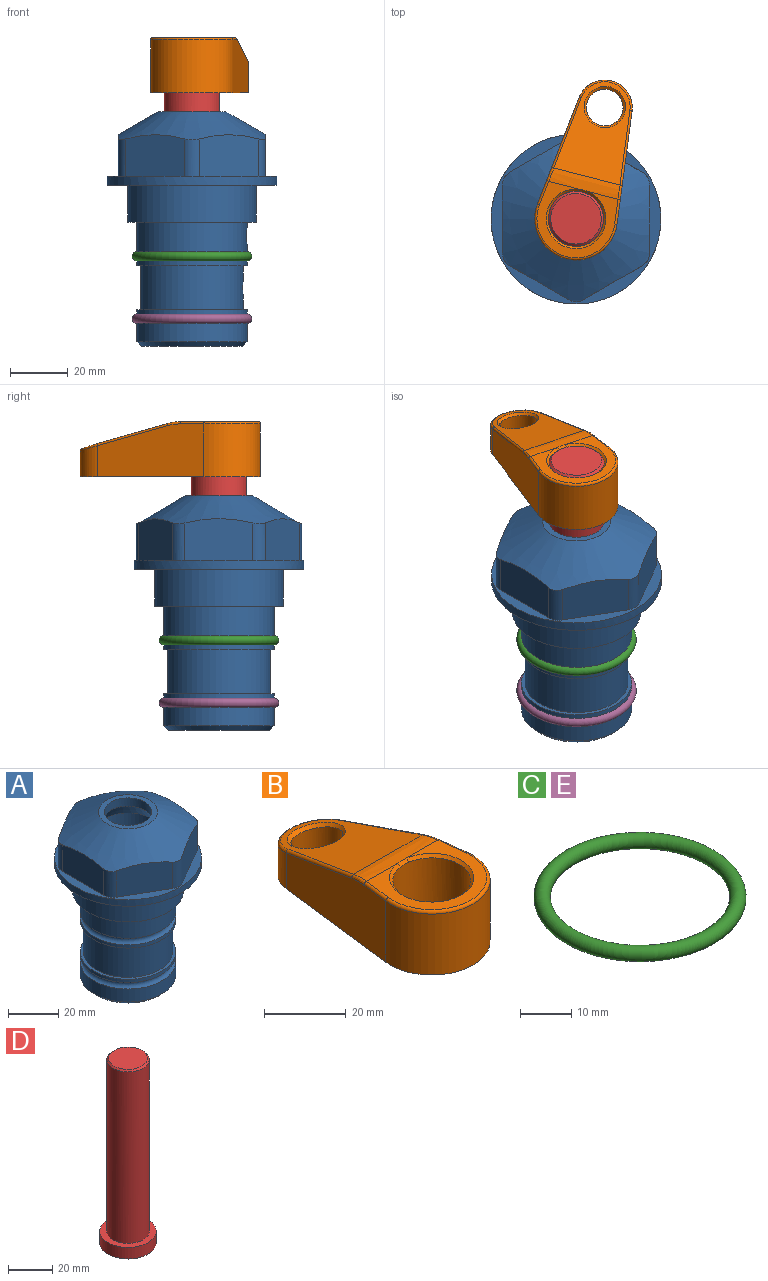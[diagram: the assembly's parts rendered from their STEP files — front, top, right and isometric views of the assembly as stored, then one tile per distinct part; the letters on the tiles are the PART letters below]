
ASSEMBLY  parts=5 mates=4
PART A: 36 faces, bbox 58.7x58.7x81 mm
  f0: cylinder r=17.78mm len=35.56mm, axis (0,0,1), area 1670.8mm2, adj f23,f24,f31
  f1: cylinder r=19.05mm len=38.1mm, axis (0,0,1), area 1191.9mm2, adj f26,f27,f30
  f2: plane 58.66x58.66mm, normal (0,0,-1), area 1150.6mm2, adj f3,f28
  f3: cylinder r=29.33mm len=58.66mm, axis (0,0,-1), area 585.1mm2, adj f2,f4
  f4: plane 58.66x58.66mm, normal (0,0,1), area 475.9mm2, adj f3,f5,f6,f7,f8,f9,f10,f11
  f5: plane 20.32x14.34mm, normal (-0.5,0.87,0), area 324.4mm2, adj f4,f15,f16,f17
  f6: plane 20.32x14.34mm, normal (0.5,0.87,0), area 324.4mm2, adj f4,f14,f15,f17
  f7: plane 23.48x14.34mm, normal (1,0,0), area 324.4mm2, adj f4,f13,f14,f17
  f8: plane 20.32x14.34mm, normal (0.5,-0.87,0), area 324.4mm2, adj f4,f12,f13,f17
  f9: plane 20.32x14.34mm, normal (-0.5,-0.87,0), area 324.4mm2, adj f4,f11,f12,f17
  f10: plane 23.48x14.34mm, normal (-1,0,0), area 324.4mm2, adj f4,f11,f16,f17
  f11: cylinder r=5.08mm len=12.85mm, axis (0,0,-1), area 67.2mm2, adj f4,f9,f10,f17
  f12: cylinder r=5.08mm len=12.85mm, axis (0,0,-1), area 67.2mm2, adj f4,f8,f9,f17
  f13: cylinder r=5.08mm len=12.85mm, axis (0,0,-1), area 67.2mm2, adj f4,f7,f8,f17
  f14: cylinder r=5.08mm len=12.85mm, axis (0,0,-1), area 67.2mm2, adj f4,f6,f7,f17
  f15: cylinder r=5.08mm len=12.85mm, axis (0,0,-1), area 67.2mm2, adj f4,f5,f6,f17
  f16: cylinder r=5.08mm len=12.85mm, axis (0,0,-1), area 67.2mm2, adj f4,f5,f10,f17
  f17: cone r=11.73mm half-angle=60deg, axis (0,0,-1), area 2071.8mm2, adj f5,f6,f7,f8,f9,f10,f11,f12
  f18: plane 23.46x23.46mm, normal (0,0,1), area 147.4mm2, adj f17,f35
  f19: plane 34.93x34.93mm, normal (0,0,-1), area 958mm2, adj f29
  f20: cylinder r=19.05mm len=38.1mm, axis (0,0,1), area 760.1mm2, adj f21,f29
  f21: torus R=19.05mm, axis (0,0,1), area 565.3mm2, adj f20,f22
  f22: cylinder r=19.05mm len=38.1mm, axis (0,0,1), area 190mm2, adj f21,f23
  f23: plane 38.1x38.1mm, normal (0,0,1), area 146.9mm2, adj f0,f22
  f24: plane 38.1x38.1mm, normal (0,0,-1), area 146.9mm2, adj f0,f25
  f25: cylinder r=19.05mm len=38.1mm, axis (0,0,1), area 190mm2, adj f24,f26
  f26: torus R=19.05mm, axis (0,0,1), area 565.3mm2, adj f1,f25
  f27: plane 44.45x44.45mm, normal (0,0,-1), area 411.7mm2, adj f1,f28
  f28: cylinder r=22.23mm len=44.45mm, axis (0,0,1), area 1773.5mm2, adj f2,f27
  f29: cone r=19.05mm half-angle=45deg, axis (0,0,1), area 257.5mm2, adj f19,f20
  f30: cylinder r=3.17mm len=6.75mm, axis (-1,0,0), area 128mm2, adj f1,f33
  f31: cylinder r=3.17mm len=6.35mm, axis (-1,0,0), area 102.5mm2, adj f0,f33
  f32: plane 25.4x25.4mm, normal (0,0,1), area 506.7mm2, adj f33
  f33: cylinder r=12.7mm len=66.42mm, axis (0,0,-1), area 5236.2mm2, adj f30,f31,f32,f34
  f34: cone r=9.53mm half-angle=30deg, axis (0,0,-1), area 443.4mm2, adj f33,f35
  f35: cylinder r=9.53mm len=19.05mm, axis (0,0,-1), area 240.9mm2, adj f18,f34
PART B: 31 faces, bbox 31.7x65.5x19.8 mm
  f0: plane 39.12x18.26mm, normal (0.99,0.12,0), area 612.2mm2, adj f1,f4,f7,f11,f13,f15
  f1: cylinder r=9.53mm len=18.91mm, axis (0,0,-1), area 296.1mm2, adj f0,f2,f7,f17
  f2: plane 39.12x18.26mm, normal (-0.99,0.12,0), area 612.2mm2, adj f1,f4,f7,f12,f14,f16
  f3: cylinder r=6.35mm len=12.7mm, axis (0,0,-1), area 362.4mm2, adj f7,f18
  f4: cylinder r=14.29mm len=28.58mm, axis (0,0,-1), area 882.2mm2, adj f0,f2,f7,f10
  f5: cylinder r=9.53mm len=19.05mm, axis (0,0,-1), area 1092.6mm2, adj f7,f19,f20
  f6: plane 26.99x23.69mm, normal (0,0,1), area 216.2mm2, adj f9,f10,f11,f12,f19
  f7: plane 63.5x28.58mm, normal (0,0,-1), area 661.8mm2, adj f0,f1,f2,f3,f4,f5,f22,f23
  f8: plane 33.52x23.6mm, normal (0,0.26,0.97), area 486mm2, adj f9,f15,f16,f17,f18
  f9: cylinder r=19.05mm len=24.72mm, axis (1,0,0), area 120.4mm2, adj f6,f8,f13,f14,f20
  f10: torus R=13.49mm, axis (0,0,1), area 59mm2, adj f4,f6,f11,f12
  f11: cylinder r=0.79mm len=8.67mm, axis (0.12,-0.99,0), area 10.8mm2, adj f0,f6,f10,f13
  f12: cylinder r=0.79mm len=8.67mm, axis (0.12,0.99,0), area 10.8mm2, adj f2,f6,f10,f14
  f13: bspline ~4.95x1.42mm, area 6.1mm2, adj f0,f9,f11,f15
  f14: bspline ~4.95x1.42mm, area 6.1mm2, adj f2,f9,f12,f16
  f15: cylinder r=0.79mm len=25.95mm, axis (0.12,-0.96,0.26), area 32.9mm2, adj f0,f8,f13,f17
  f16: cylinder r=0.79mm len=25.95mm, axis (0.12,0.96,-0.26), area 32.9mm2, adj f2,f8,f14,f17
  f17: bspline ~18.91x8.38mm, area 30mm2, adj f1,f8,f15,f16
  f18: bspline ~14.29x14.29mm, area 48.3mm2, adj f3,f8
  f19: cone r=9.53mm half-angle=45deg, axis (0,0,1), area 66.5mm2, adj f5,f6,f20
  f20: bspline ~3.22x0.96mm, area 3.5mm2, adj f5,f9,f19
  f21: plane 2.75x2.72mm, normal (0,0,-1), area 2.9mm2, adj f23,f25,f28
  f22: plane 23.05x15.88mm, normal (-0.99,-0.12,0), area 323.6mm2, adj f7,f25,f26,f27,f28,f29
  f23: plane 23.05x15.88mm, normal (0.99,-0.12,0), area 323.6mm2, adj f7,f21,f25,f27,f28,f30
  f24: cylinder r=9.53mm len=10.69mm, axis (0,0,-1), area 114.7mm2, adj f7,f27,f29,f30
  f25: cylinder r=12.7mm len=20.59mm, axis (0,0,-1), area 381.1mm2, adj f7,f21,f22,f23,f26,f28
  f26: plane 2.75x2.72mm, normal (0,0,-1), area 2.9mm2, adj f22,f25,f28
  f27: plane 19.72x18.37mm, normal (0,-0.26,-0.97), area 291.8mm2, adj f22,f23,f24,f28,f29,f30
  f28: cylinder r=15.88mm len=19.92mm, axis (1,0,0), area 54.8mm2, adj f21,f22,f23,f25,f26,f27
  f29: cylinder r=1.59mm len=11mm, axis (0,0,-1), area 34.7mm2, adj f7,f22,f24,f27
  f30: cylinder r=1.59mm len=11mm, axis (0,0,-1), area 34.7mm2, adj f7,f23,f24,f27
PART C: 1 faces, bbox 44.7x44.7x3.2 mm
  f0: torus R=19.05mm, axis (0,0,1), area 1193.9mm2
PART D: 6 faces, bbox 25.4x25.4x101.6 mm
  f0: plane 17.46x17.46mm, normal (0,0,1), area 239.5mm2, adj f5
  f1: plane 25.4x25.4mm, normal (0,0,-1), area 506.7mm2, adj f2
  f2: cylinder r=12.7mm len=25.4mm, axis (0,0,1), area 506.7mm2, adj f1,f3
  f3: plane 25.4x25.4mm, normal (0,0,1), area 221.7mm2, adj f2,f4
  f4: cylinder r=9.53mm len=94.46mm, axis (0,0,1), area 5653mm2, adj f3,f5
  f5: cone r=8.73mm half-angle=45deg, axis (0,0,-1), area 64.4mm2, adj f0,f4
PART E: same geometry as C
PLACE A at identity fixed
PLACE B rot(axis=(0,0,-1),14.5deg) t=(0,0,-12.45)mm
PLACE C at identity
PLACE D rot(axis=(0,0,-1),14.5deg) t=(0,0,-12.45)mm
PLACE E t=(0,0,-21.59)mm
MATE fastened E.f0 <-> A.f0  axis (0,0,1) through (0,0,-46.1)mm
MATE fastened C.f0 <-> A.f0  axis (0,0,1) through (0,0,-24.51)mm
MATE cylindrical D.f2 <-> A.f0  axis (0,0,-1) through (0,0,-50.55)mm
MATE fastened B.f4 <-> D.f2  axis (0,0,1) through (0,0,51.05)mm
